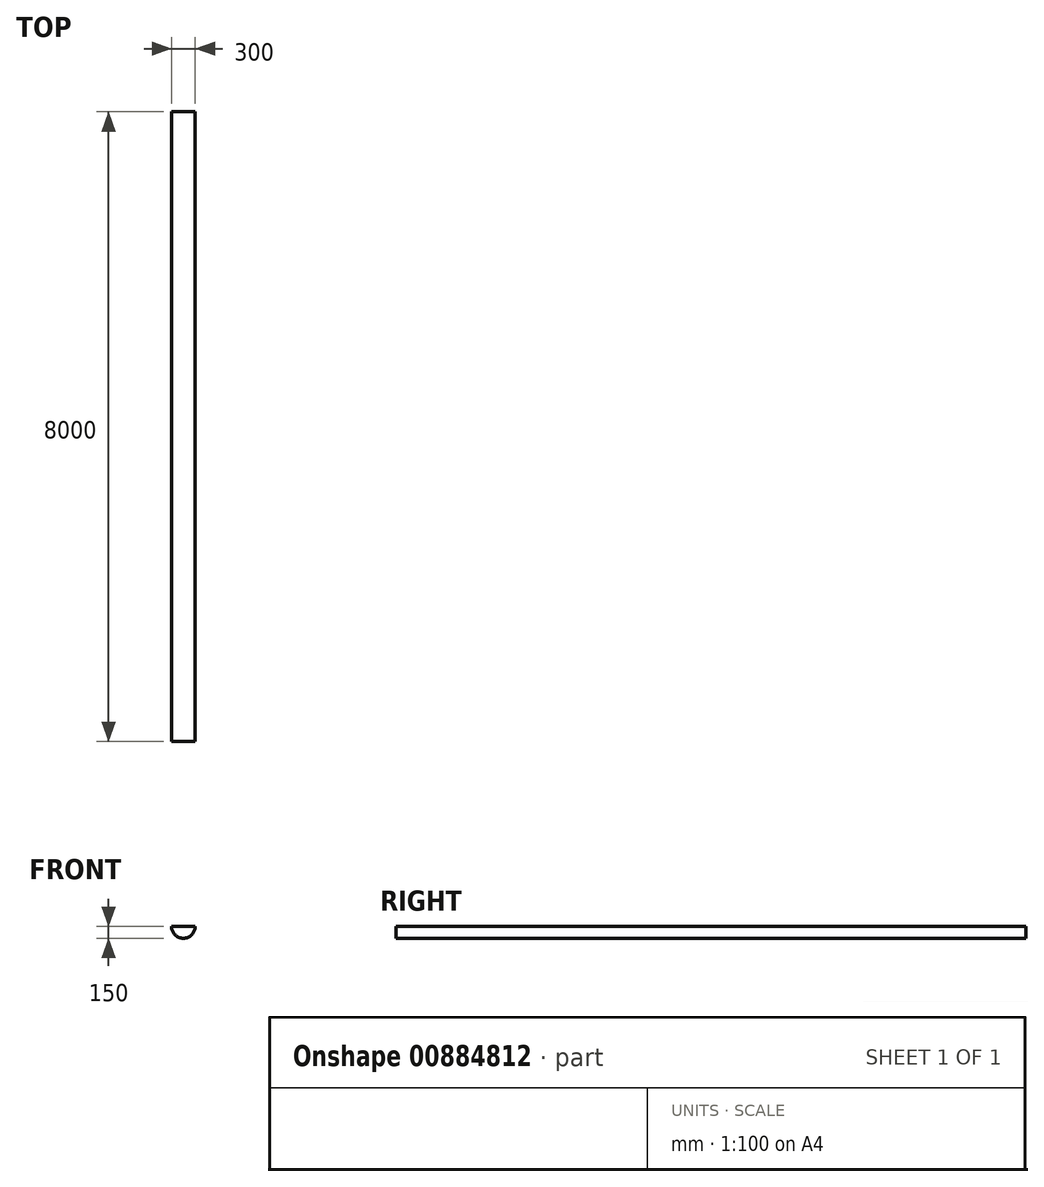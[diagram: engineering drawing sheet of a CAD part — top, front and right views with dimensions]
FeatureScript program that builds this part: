
annotation { "Feature Type Name" : "Feature", "Feature Type Description" : "" }
export const myFeature = defineFeature(function(context is Context, id is Id, definition is map)
    precondition{}
    {
        {
            var Q0;
            Q0=qCreatedBy(makeId("Front.planeOp"),FACE);
            var sketch = newSketch(context, id + "F0", { "sketchPlane" : qUnion([Q0])});
            skArc(sketch, "E0", {"start": v(-150, 50) * mm, "mid": v(0, -100) * mm, "end": v(150, 50) * mm});
            skLineSegment(sketch, "E1", {"start": v(150, 50) * mm, "end": v(-150, 50) * mm});
            skSolve(sketch);
        }
        {
            var Q0;
            Q0 = qSketchRegion(id + "F0", true);
            extrude(context, id + "F1", {"entities" : qUnion([Q0]), "depth" : 4000 * mm, "offsetDistance" : 25 * mm, "hasSecondDirection" : true, "secondDirectionOppositeDirection" : true, "secondDirectionDepth" : 4000 * mm});
        }
    });
